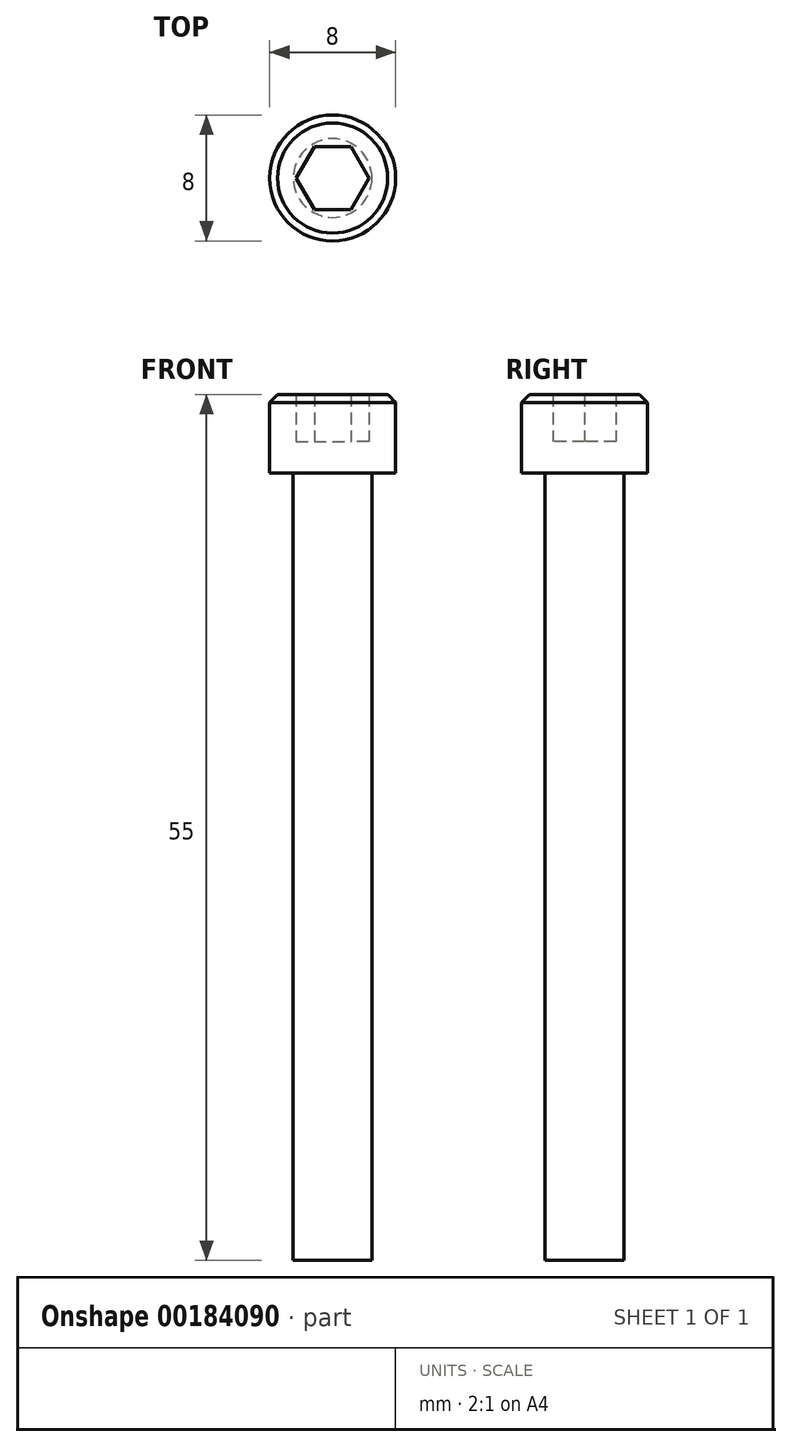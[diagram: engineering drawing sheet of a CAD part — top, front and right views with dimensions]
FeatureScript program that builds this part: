
annotation { "Feature Type Name" : "Feature", "Feature Type Description" : "" }
export const myFeature = defineFeature(function(context is Context, id is Id, definition is map)
    precondition{}
    {
        {
            var Q0;
            Q0=qCreatedBy(makeId("Top.planeOp"),FACE);
            var sketch = newSketch(context, id + "F0", { "sketchPlane" : qUnion([Q0])});
            skCircle(sketch, "E0", {"center": v(0, 0) * mm, "radius": 2.5 * mm});
            skCircle(sketch, "E1", {"center": v(0, 0) * mm, "radius": 4 * mm});
            skCircle(sketch, "E2.cCircle", {"center": v(0, 0) * mm, "radius": 2 * mm, "construction": true});
            skLineSegment(sketch, "E2.0", {"start": v(1.15, -2) * mm, "end": v(-1.15, -2) * mm});
            skLineSegment(sketch, "E2.1", {"start": v(-1.15, -2) * mm, "end": v(-2.3, 0) * mm});
            skLineSegment(sketch, "E2.2", {"start": v(-2.3, 0) * mm, "end": v(-1.15, 2) * mm});
            skLineSegment(sketch, "E2.3", {"start": v(-1.15, 2) * mm, "end": v(1.15, 2) * mm});
            skLineSegment(sketch, "E2.4", {"start": v(1.15, 2) * mm, "end": v(2.3, 0) * mm});
            skLineSegment(sketch, "E2.5", {"start": v(2.3, 0) * mm, "end": v(1.15, -2) * mm});
            skPoint(sketch, "E2.0.midPoint", {"position": v(0, -2) * mm});
            skSolve(sketch);
        }
        {
            var Q0;
            Q0=makeQuery(id+"F0.imprint","IMPRINT",FACE,{"disambiguationData":[TD([[makeQuery(id+"F0.imprint","IMPRINT",EDGE,{"derivedFrom":sQuery(id+"F0.wireOp",EDGE,"E0")}),-1.0]])]});
            var Q1;
            Q1=makeQuery(id+"F0.imprint","IMPRINT",FACE,{"disambiguationData":[TD([[makeQuery(id+"F0.imprint","IMPRINT",EDGE,{"derivedFrom":sQuery(id+"F0.wireOp",EDGE,"E0")}),1.0]])]});
            var Q2;
            Q2=makeQuery(id+"F0.imprint","IMPRINT",FACE,{"disambiguationData":[TD([[makeQuery(id+"F0.imprint","IMPRINT",EDGE,{"derivedFrom":sQuery(id+"F0.wireOp",EDGE,"E2.0")}),-1.0]])]});
            extrude(context, id + "F1", {"entities" : qUnion([Q0, Q1, Q2]), "depth" : 5 * mm});
        }
        {
            var Q0;
            Q0=makeQuery(id+"F0.imprint","IMPRINT",FACE,{"disambiguationData":[TD([[makeQuery(id+"F0.imprint","IMPRINT",EDGE,{"derivedFrom":sQuery(id+"F0.wireOp",EDGE,"E2.0")}),-1.0]])]});
            var Q1;
            Q1=makeQuery(id+"F1.opExtrude","CAP_FACE",FACE,{"disambiguationData":[OSD([sQuery(id+"F0.wireOp",EDGE,"E1")])],"isStart":false});
            extrude(context, id + "F2", {"entities" : qUnion([Q0]), "operationType" : NewBodyOperationType.REMOVE, "endBound" : BoundingType.UP_TO_SURFACE, "endBoundEntityFace" : qUnion([Q1]), "depth" : 25 * mm, "hasSecondDirection" : true, "secondDirectionOppositeDirection" : false, "secondDirectionDepth" : 2 * mm});
        }
        {
            var Q0;
            Q0=makeQuery(id+"F0.imprint","IMPRINT",FACE,{"disambiguationData":[TD([[makeQuery(id+"F0.imprint","IMPRINT",EDGE,{"derivedFrom":sQuery(id+"F0.wireOp",EDGE,"E0")}),1.0]])]});
            var Q1;
            Q1=makeQuery(id+"F0.imprint","IMPRINT",FACE,{"disambiguationData":[TD([[makeQuery(id+"F0.imprint","IMPRINT",EDGE,{"derivedFrom":sQuery(id+"F0.wireOp",EDGE,"E2.0")}),-1.0]])]});
            extrude(context, id + "F3", {"entities" : qUnion([Q0, Q1]), "operationType" : NewBodyOperationType.ADD, "oppositeDirection" : true, "depth" : 50 * mm});
        }
        {
            var Q0;
            Q0=makeQuery(id+"F1.opExtrude","CAP_EDGE",EDGE,{"disambiguationData":[OSD([sQuery(id+"F0.wireOp",EDGE,"E1")])],"isStart":false});
            chamfer(context, id + "F4", {"entities" : qUnion([Q0]), "width" : .5 * mm, "tangentPropagation" : true});
        }
    });
